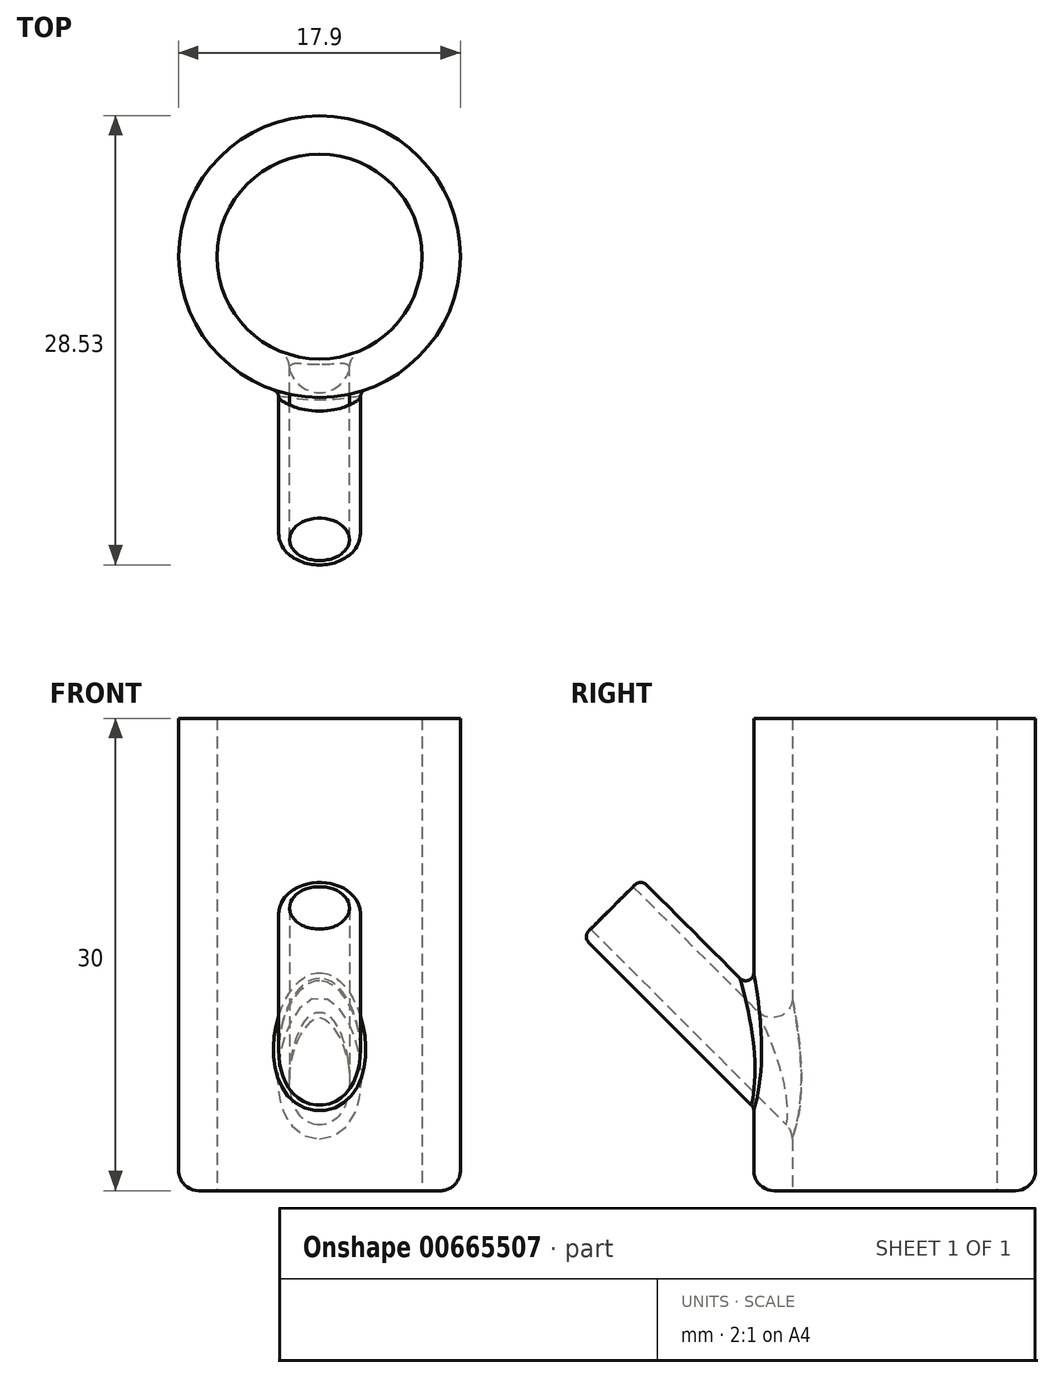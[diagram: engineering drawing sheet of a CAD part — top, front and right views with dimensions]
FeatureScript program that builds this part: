
annotation { "Feature Type Name" : "Feature", "Feature Type Description" : "" }
export const myFeature = defineFeature(function(context is Context, id is Id, definition is map)
    precondition{}
    {
        {
            var Q0;
            Q0=qCreatedBy(makeId("Top.planeOp"),FACE);
            var sketch = newSketch(context, id + "F0", { "sketchPlane" : qUnion([Q0])});
            skCircle(sketch, "E0", {"center": v(0, 0) * mm, "radius": 6.5 * mm});
            skCircle(sketch, "E1", {"center": v(0, 0) * mm, "radius": 8.95 * mm});
            skSolve(sketch);
        }
        {
            var Q0;
            Q0=makeQuery(id+"F0.imprint","IMPRINT",FACE,{"disambiguationData":[TD([[makeQuery(id+"F0.imprint","IMPRINT",EDGE,{"derivedFrom":sQuery(id+"F0.wireOp",EDGE,"E0")}),-1.0]])]});
            var Q1;
            Q1=sQuery(id+"F0.wireOp",EDGE,"E1");
            var Q2;
            Q2=sQuery(id+"F0.wireOp",EDGE,"E0");
            extrude(context, id + "F1", {"entities" : qUnion([Q0]), "surfaceEntities" : qUnion([Q1, Q2]), "depth" : 30 * mm, "offsetDistance" : 25.4 * mm, "hasSecondDirection" : true, "secondDirectionOppositeDirection" : true, "secondDirectionDepth" : 0 * mm});
        }
        {
            var Q0;
            Q0=qCreatedBy(makeId("Top.planeOp"),FACE);
            var sketch = newSketch(context, id + "F2", { "sketchPlane" : qUnion([Q0])});
            skLineSegment(sketch, "E2", {"start": v(-6, 0) * mm, "end": v(-16.07, 0) * mm, "construction": true});
            skLineSegment(sketch, "E3", {"start": v(-6.33, 0) * mm, "end": v(-16.07, 0) * mm});
            skSolve(sketch);
        }
        {
            var Q0;
            Q0=sQuery(id+"F2.wireOp",EDGE,"E2");
            cPlane(context, id + "F3", {"entities" : qUnion([Q0]), "cplaneType" : CPlaneType.LINE_ANGLE, "offset" : 25.4 * mm, "angle" : 45 * degree, "width" : 152.4 * mm, "height" : 152.4 * mm});
        }
        {
            var Q0;
            Q0=qCreatedBy(id+"F3.planeOp",FACE);
            var sketch = newSketch(context, id + "F4", { "sketchPlane" : qUnion([Q0])});
            skCircle(sketch, "E4", {"center": v(0, 0) * mm, "radius": 2.6 * mm});
            skCircle(sketch, "E5", {"center": v(0, 0) * mm, "radius": 1.9 * mm});
            skSolve(sketch);
        }
        {
            var Q0;
            Q0=makeQuery(id+"F4.imprint","IMPRINT",FACE,{"disambiguationData":[TD([[makeQuery(id+"F4.imprint","IMPRINT",EDGE,{"derivedFrom":sQuery(id+"F4.wireOp",EDGE,"E4")}),1.0]])]});
            var Q1;
            Q1=sQuery(id+"F4.wireOp",EDGE,"E4");
            extrude(context, id + "F5", {"entities" : qUnion([Q0]), "operationType" : NewBodyOperationType.ADD, "surfaceEntities" : qUnion([Q1]), "depth" : 25.4 * mm, "offsetDistance" : 25.4 * mm});
        }
        {
            var Q0;
            Q0=makeQuery(id+"F1.opExtrude","CAP_FACE",FACE,{"disambiguationData":[OSD([sQuery(id+"F0.wireOp",EDGE,"E0"),sQuery(id+"F0.wireOp",EDGE,"E1")])],"isStart":false});
            var sketch = newSketch(context, id + "F6", { "sketchPlane" : qUnion([Q0])});
            skCircle(sketch, "E6.0", {"center": v(0, 0) * mm, "radius": 6.5 * mm});
            skSolve(sketch);
        }
        {
            var Q0;
            Q0 = qSketchRegion(id + "F6", true);
            extrude(context, id + "F7", {"entities" : qUnion([Q0]), "operationType" : NewBodyOperationType.REMOVE, "endBound" : BoundingType.THROUGH_ALL, "oppositeDirection" : true, "depth" : 25.4 * mm, "offsetDistance" : 25.4 * mm});
        }
        {
            var Q0;
            Q0=makeQuery(id+"F5.opExtrude","CAP_FACE",FACE,{"disambiguationData":[OSD([sQuery(id+"F4.wireOp",EDGE,"E4"),sQuery(id+"F4.wireOp",EDGE,"E5")])],"isStart":false});
            var sketch = newSketch(context, id + "F8", { "sketchPlane" : qUnion([Q0])});
            skCircle(sketch, "E7.0", {"center": v(0, 0) * mm, "radius": 1.9 * mm});
            skSolve(sketch);
        }
        {
            var Q0;
            Q0=makeQuery(id+"F8.imprint","IMPRINT",FACE,{"disambiguationData":[TD([[makeQuery(id+"F8.imprint","IMPRINT",EDGE,{"derivedFrom":sQuery(id+"F8.wireOp",EDGE,"E7.0")}),1.0]])]});
            extrude(context, id + "F9", {"entities" : qUnion([Q0]), "operationType" : NewBodyOperationType.REMOVE, "oppositeDirection" : true, "depth" : 25.4 * mm, "offsetDistance" : 25.4 * mm});
        }
        {
            var Q0;
            {var subQ0=sQuery(id+"F4.wireOp",EDGE,"E4");Q0=makeQuery(id+"F5.boolean.opBoolean","SPLIT",FACE,{"disambiguationData":[TD([makeQuery(id+"F1.opExtrude","SWEPT_FACE",FACE,{"disambiguationData":[OSD([sQuery(id+"F0.wireOp",EDGE,"E1")])]}),makeQuery(id+"F5.opExtrude","CAP_FACE",FACE,{"disambiguationData":[OSD([subQ0,sQuery(id+"F4.wireOp",EDGE,"E5")])],"isStart":false})])],"derivedFrom":makeQuery(id+"F5.opExtrude","SWEPT_FACE",FACE,{"disambiguationData":[OSD([subQ0])]})});}
            fillet(context, id + "F10", {"entities" : qUnion([Q0]), "radius" : 0.5 * mm, "allowEdgeOverflow" : false});
        }
        {
            var Q0;
            Q0=makeQuery(id+"F1.opExtrude","CAP_EDGE",EDGE,{"disambiguationData":[OSD([sQuery(id+"F0.wireOp",EDGE,"E1")])],"isStart":true});
            var Q1;
            {var subQ1=sQuery(id+"F0.wireOp",EDGE,"E0");var subQ2=sQuery(id+"F4.wireOp",EDGE,"E5");var subQ3=sQuery(id+"F4.wireOp",EDGE,"E4");var subQ4=makeQuery(id+"F1.opExtrude","SWEPT_FACE",FACE,{"disambiguationData":[OSD([subQ1])]});Q1=makeQuery(id+"F9.boolean.opBoolean","INTERSECT",EDGE,{"derivedFrom":[makeQuery(id+"F7.boolean.opBoolean","MERGE",FACE,{"derivedFrom":[makeQuery(id+"F5.boolean.opBoolean","SPLIT",FACE,{"disambiguationData":[TD([makeQuery(id+"F5.opExtrude","SWEPT_FACE",FACE,{"disambiguationData":[OSD([subQ2])]})])],"derivedFrom":subQ4}),makeQuery(id+"F5.boolean.opBoolean","SPLIT",FACE,{"disambiguationData":[TD([makeQuery(id+"F5.opExtrude","SWEPT_FACE",FACE,{"disambiguationData":[OSD([subQ3])]})])],"derivedFrom":subQ4}),makeQuery(id+"F7.opExtrude","SWEPT_FACE",FACE,{"disambiguationData":[OSD([sQuery(id+"F6.wireOp",EDGE,"E6.0")])]})]}),makeQuery(id+"F9.opExtrude","SWEPT_FACE",FACE,{"disambiguationData":[OSD([sQuery(id+"F8.wireOp",EDGE,"E7.0")])]})]});}
            fillet(context, id + "F11", {"entities" : qUnion([Q0, Q1]), "radius" : 1.27 * mm, "tangentPropagation" : true, "allowEdgeOverflow" : false});
        }
    });
